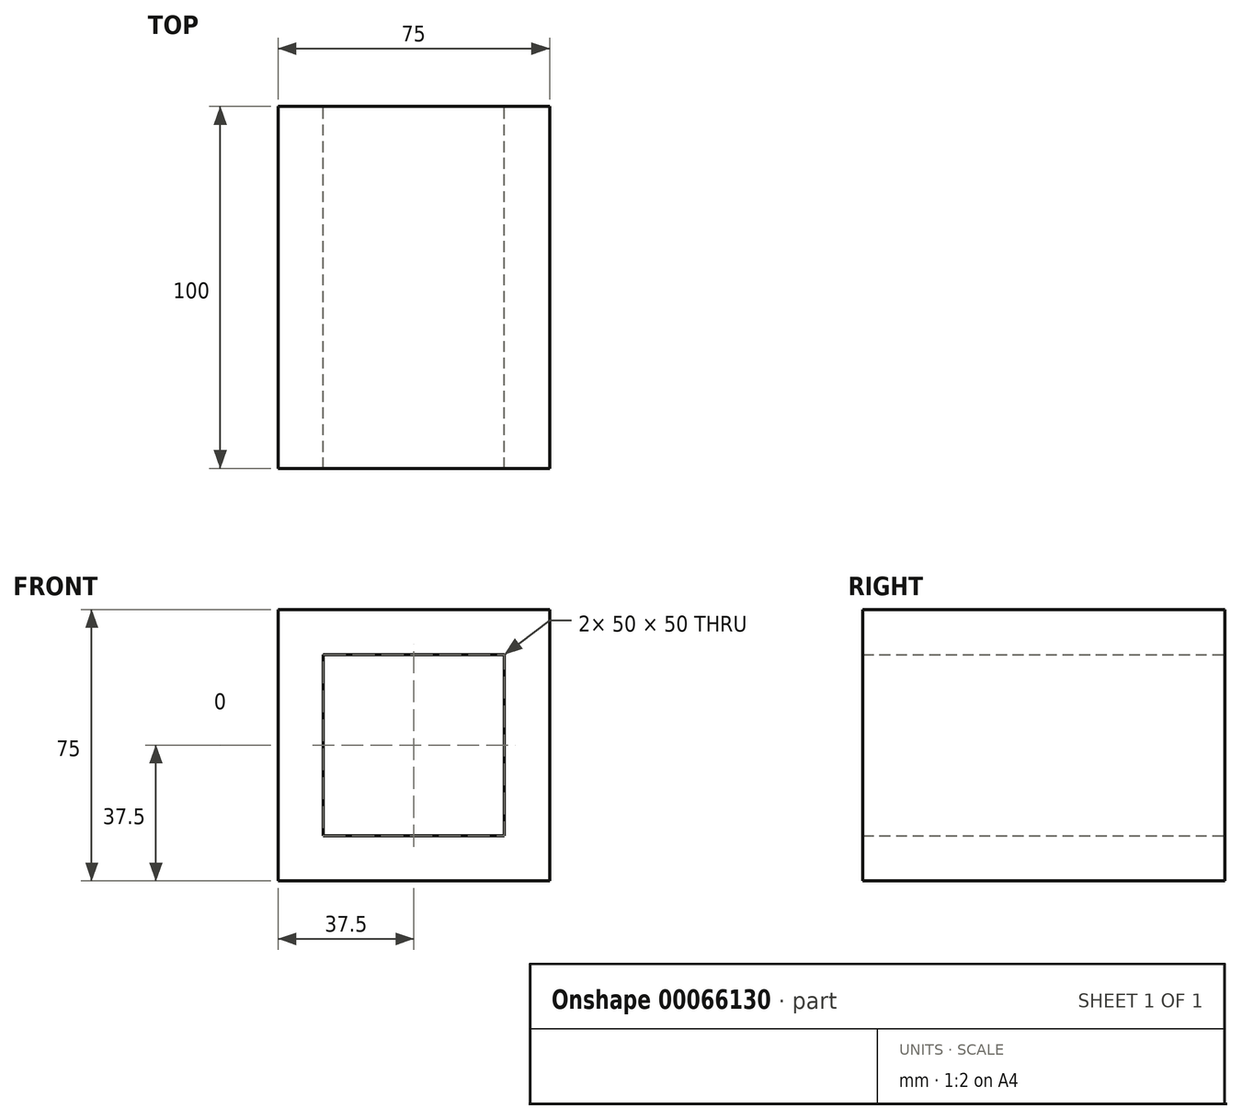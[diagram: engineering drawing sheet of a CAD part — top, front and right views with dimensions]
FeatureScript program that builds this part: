
annotation { "Feature Type Name" : "Feature", "Feature Type Description" : "" }
export const myFeature = defineFeature(function(context is Context, id is Id, definition is map)
    precondition{}
    {
        {
            var Q0;
            Q0=qCreatedBy(makeId("Front.planeOp"),FACE);
            var sketch = newSketch(context, id + "F0", { "sketchPlane" : qUnion([Q0])});
            skLineSegment(sketch, "E0.rect.bottom", {"start": v(25, 25) * mm, "end": v(-25, 25) * mm});
            skLineSegment(sketch, "E0.rect.top", {"start": v(25, -25) * mm, "end": v(-25, -25) * mm});
            skLineSegment(sketch, "E0.rect.left", {"start": v(25, 25) * mm, "end": v(25, -25) * mm});
            skLineSegment(sketch, "E0.rect.right", {"start": v(-25, 25) * mm, "end": v(-25, -25) * mm});
            skPoint(sketch, "E0.rect.middle", {"position": v(0, 0) * mm});
            skLineSegment(sketch, "E1.rect.bottom", {"start": v(-37.5, 37.5) * mm, "end": v(37.5, 37.5) * mm});
            skLineSegment(sketch, "E1.rect.top", {"start": v(-37.5, -37.5) * mm, "end": v(37.5, -37.5) * mm});
            skLineSegment(sketch, "E1.rect.left", {"start": v(-37.5, 37.5) * mm, "end": v(-37.5, -37.5) * mm});
            skLineSegment(sketch, "E1.rect.right", {"start": v(37.5, 37.5) * mm, "end": v(37.5, -37.5) * mm});
            skSolve(sketch);
        }
        {
            var Q0;
            Q0 = qSketchRegion(id + "F0", true);
            extrude(context, id + "F1", {"entities" : qUnion([Q0]), "depth" : 100 * mm});
        }
    });
